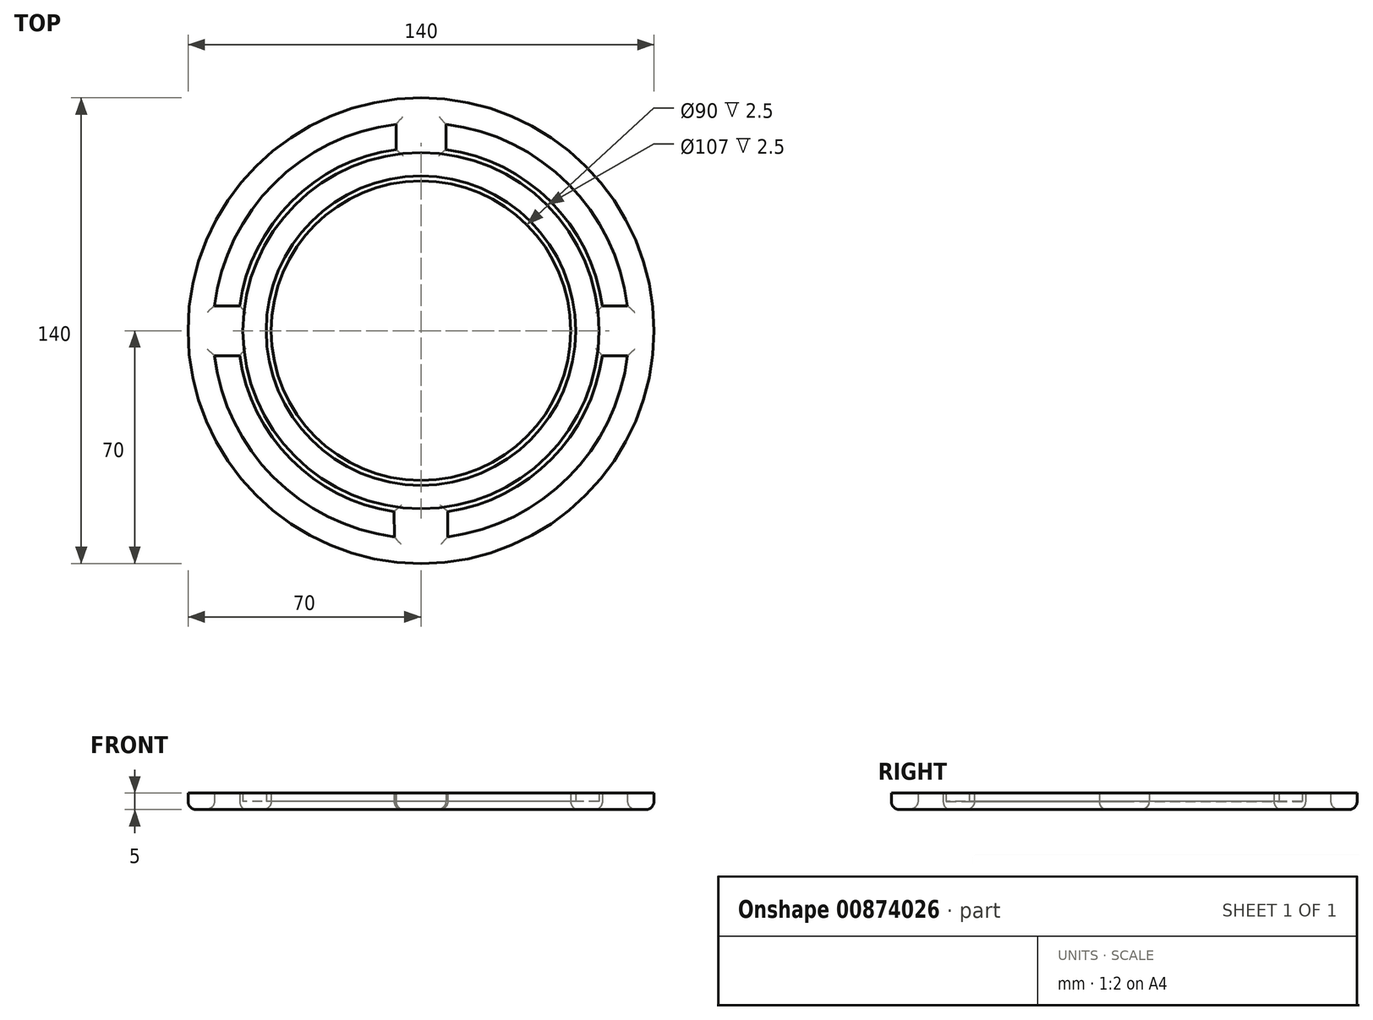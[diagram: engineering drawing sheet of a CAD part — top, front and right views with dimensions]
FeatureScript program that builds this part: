
annotation { "Feature Type Name" : "Feature", "Feature Type Description" : "" }
export const myFeature = defineFeature(function(context is Context, id is Id, definition is map)
    precondition{}
    {
        {
            var Q0;
            Q0=qCreatedBy(makeId("Top.planeOp"),FACE);
            var sketch = newSketch(context, id + "F0", { "sketchPlane" : qUnion([Q0])});
            skCircle(sketch, "E0", {"center": v(0, 0) * mm, "radius": 45 * mm});
            skCircle(sketch, "E1", {"center": v(0, 0) * mm, "radius": 46.5 * mm});
            skArc(sketch, "E2", {"start": v(8.01, -61.98) * mm, "mid": v(44.38, -44.01) * mm, "end": v(62.05, -7.5) * mm});
            skCircle(sketch, "E3", {"center": v(0, 0) * mm, "radius": 70 * mm});
            skArc(sketch, "E4", {"start": v(8.09, -54.4) * mm, "mid": v(39.1, -38.68) * mm, "end": v(54.49, -7.5) * mm});
            skLineSegment(sketch, "E5.left", {"start": v(-7.5, 62.05) * mm, "end": v(-7.5, 54.49) * mm});
            skLineSegment(sketch, "E5.right", {"start": v(7.5, 62.05) * mm, "end": v(7.5, 54.49) * mm});
            skLineSegment(sketch, "E6.bottom", {"start": v(-62.05, 7.5) * mm, "end": v(-54.49, 7.5) * mm});
            skLineSegment(sketch, "E6.top", {"start": v(-62.05, -7.5) * mm, "end": v(-54.49, -7.5) * mm});
            skLineSegment(sketch, "E7.trimOffspring", {"start": v(54.49, 7.5) * mm, "end": v(62.05, 7.5) * mm});
            skLineSegment(sketch, "E8.trimOffspring", {"start": v(54.49, -7.5) * mm, "end": v(62.05, -7.5) * mm});
            skLineSegment(sketch, "E9.trimOffspring", {"start": v(8.09, -54.4) * mm, "end": v(8.01, -61.98) * mm});
            skLineSegment(sketch, "E10.trimOffspring", {"start": v(-8.09, -54.4) * mm, "end": v(-8.01, -61.98) * mm});
            skArc(sketch, "E11.trimOffspring", {"start": v(62.05, 7.5) * mm, "mid": v(44.2, 44.2) * mm, "end": v(7.5, 62.05) * mm});
            skArc(sketch, "E12.trimOffspring", {"start": v(54.49, 7.5) * mm, "mid": v(38.9, 38.9) * mm, "end": v(7.5, 54.49) * mm});
            skArc(sketch, "E13.trimOffspring", {"start": v(-62.05, -7.5) * mm, "mid": v(-44.38, -44.01) * mm, "end": v(-8.01, -61.98) * mm});
            skArc(sketch, "E14.trimOffspring", {"start": v(-54.49, -7.5) * mm, "mid": v(-39.1, -38.68) * mm, "end": v(-8.09, -54.4) * mm});
            skArc(sketch, "E15.trimOffspring", {"start": v(-7.5, 62.05) * mm, "mid": v(-44.2, 44.2) * mm, "end": v(-62.05, 7.5) * mm});
            skArc(sketch, "E16.trimOffspring", {"start": v(-7.5, 54.49) * mm, "mid": v(-38.9, 38.9) * mm, "end": v(-54.49, 7.5) * mm});
            skCircle(sketch, "E17", {"center": v(0, 0) * mm, "radius": 53.5 * mm});
            skSolve(sketch);
        }
        {
            var Q0;
            Q0=makeQuery(id+"F0.imprint","IMPRINT",FACE,{"disambiguationData":[TD([[makeQuery(id+"F0.imprint","IMPRINT",EDGE,{"derivedFrom":sQuery(id+"F0.wireOp",EDGE,"E2")}),-1.0]])]});
            var Q1;
            Q1=makeQuery(id+"F0.imprint","IMPRINT",FACE,{"disambiguationData":[TD([[makeQuery(id+"F0.imprint","IMPRINT",EDGE,{"derivedFrom":sQuery(id+"F0.wireOp",EDGE,"E0")}),-1.0]])]});
            extrude(context, id + "F1", {"entities" : qUnion([Q0, Q1]), "depth" : 5 * mm, "offsetDistance" : 25 * mm});
        }
        {
            var Q0;
            Q0=makeQuery(id+"F0.imprint","IMPRINT",FACE,{"disambiguationData":[TD([[makeQuery(id+"F0.imprint","IMPRINT",EDGE,{"derivedFrom":sQuery(id+"F0.wireOp",EDGE,"E1")}),-1.0]])]});
            extrude(context, id + "F2", {"entities" : qUnion([Q0]), "depth" : 2.5 * mm, "offsetDistance" : 25 * mm});
        }
        {
            var Q0;
            Q0=makeQuery(id+"F1.opExtrude","SWEPT_BODY",BODY,{"disambiguationData":[OSD([sQuery(id+"F0.wireOp",EDGE,"E0"),sQuery(id+"F0.wireOp",EDGE,"E1")])]});
            var Q1;
            Q1=makeQuery(id+"F1.opExtrude","SWEPT_BODY",BODY,{"disambiguationData":[OSD([sQuery(id+"F0.wireOp",EDGE,"E2"),sQuery(id+"F0.wireOp",EDGE,"E3"),sQuery(id+"F0.wireOp",EDGE,"E4"),sQuery(id+"F0.wireOp",EDGE,"E5.left"),sQuery(id+"F0.wireOp",EDGE,"E5.right"),sQuery(id+"F0.wireOp",EDGE,"E6.bottom"),sQuery(id+"F0.wireOp",EDGE,"E6.top"),sQuery(id+"F0.wireOp",EDGE,"E7.trimOffspring"),sQuery(id+"F0.wireOp",EDGE,"E8.trimOffspring"),sQuery(id+"F0.wireOp",EDGE,"E9.trimOffspring"),sQuery(id+"F0.wireOp",EDGE,"E10.trimOffspring"),sQuery(id+"F0.wireOp",EDGE,"E11.trimOffspring"),sQuery(id+"F0.wireOp",EDGE,"E12.trimOffspring"),sQuery(id+"F0.wireOp",EDGE,"E13.trimOffspring"),sQuery(id+"F0.wireOp",EDGE,"E14.trimOffspring"),sQuery(id+"F0.wireOp",EDGE,"E15.trimOffspring"),sQuery(id+"F0.wireOp",EDGE,"E16.trimOffspring"),sQuery(id+"F0.wireOp",EDGE,"E17")])]});
            var Q2;
            Q2=makeQuery(id+"F2.opExtrude","SWEPT_BODY",BODY,{"disambiguationData":[OSD([sQuery(id+"F0.wireOp",EDGE,"E1"),sQuery(id+"F0.wireOp",EDGE,"E17")])]});
            booleanBodies(context, id + "F3", {"operationType" : BooleanOperationType.UNION, "tools" : qUnion([Q0, Q1, Q2])});
        }
        {
            var Q0;
            {var subQ0=sQuery(id+"F0.wireOp",EDGE,"E17");var subQ1=sQuery(id+"F0.wireOp",EDGE,"E1");Q0=makeQuery(id+"F3.opBoolean","MERGE",FACE,{"derivedFrom":[makeQuery(id+"F1.opExtrude","CAP_FACE",FACE,{"disambiguationData":[OSD([sQuery(id+"F0.wireOp",EDGE,"E0"),subQ1])],"isStart":true}),makeQuery(id+"F1.opExtrude","CAP_FACE",FACE,{"disambiguationData":[OSD([sQuery(id+"F0.wireOp",EDGE,"E2"),sQuery(id+"F0.wireOp",EDGE,"E3"),sQuery(id+"F0.wireOp",EDGE,"E4"),sQuery(id+"F0.wireOp",EDGE,"E5.left"),sQuery(id+"F0.wireOp",EDGE,"E5.right"),sQuery(id+"F0.wireOp",EDGE,"E6.bottom"),sQuery(id+"F0.wireOp",EDGE,"E6.top"),sQuery(id+"F0.wireOp",EDGE,"E7.trimOffspring"),sQuery(id+"F0.wireOp",EDGE,"E8.trimOffspring"),sQuery(id+"F0.wireOp",EDGE,"E9.trimOffspring"),sQuery(id+"F0.wireOp",EDGE,"E10.trimOffspring"),sQuery(id+"F0.wireOp",EDGE,"E11.trimOffspring"),sQuery(id+"F0.wireOp",EDGE,"E12.trimOffspring"),sQuery(id+"F0.wireOp",EDGE,"E13.trimOffspring"),sQuery(id+"F0.wireOp",EDGE,"E14.trimOffspring"),sQuery(id+"F0.wireOp",EDGE,"E15.trimOffspring"),sQuery(id+"F0.wireOp",EDGE,"E16.trimOffspring"),subQ0])],"isStart":true}),makeQuery(id+"F2.opExtrude","CAP_FACE",FACE,{"disambiguationData":[OSD([subQ1,subQ0])],"isStart":true})]});}
            fillet(context, id + "F4", {"entities" : qUnion([Q0]), "radius" : 2.5 * mm, "tangentPropagation" : true, "allowEdgeOverflow" : false});
        }
    });
